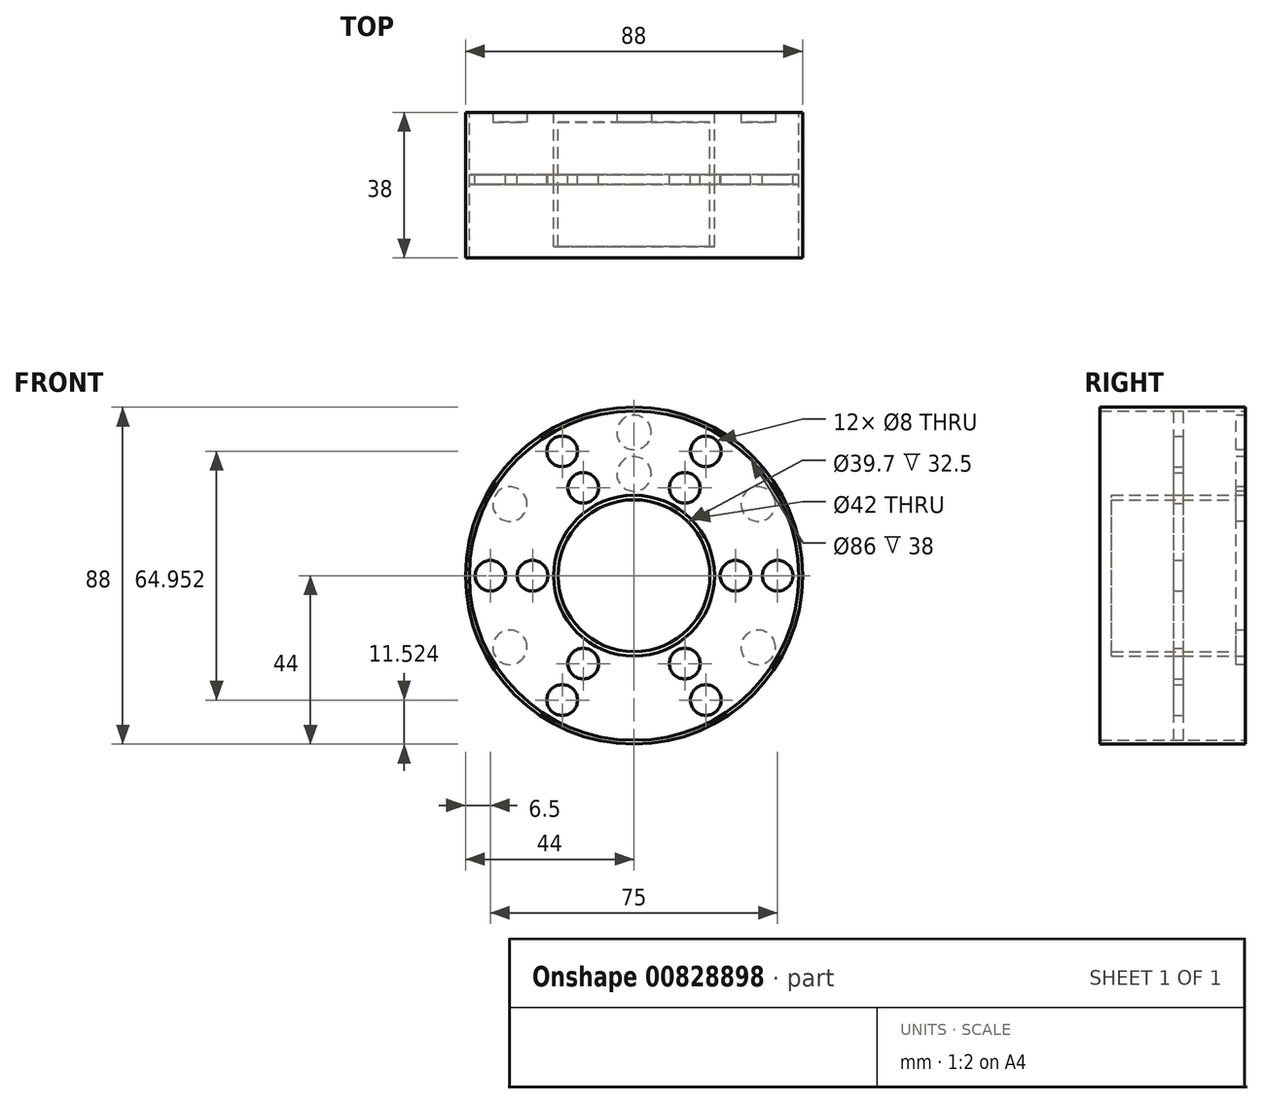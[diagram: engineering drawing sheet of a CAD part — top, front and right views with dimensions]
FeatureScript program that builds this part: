
annotation { "Feature Type Name" : "Feature", "Feature Type Description" : "" }
export const myFeature = defineFeature(function(context is Context, id is Id, definition is map)
    precondition{}
    {
        {
            var Q0;
            Q0=qCreatedBy(makeId("Front.planeOp"),FACE);
            var sketch = newSketch(context, id + "F0", { "sketchPlane" : qUnion([Q0])});
            skCircle(sketch, "E0", {"center": v(0, 0) * mm, "radius": 44 * mm});
            skCircle(sketch, "E1", {"center": v(0, 0) * mm, "radius": 19.85 * mm});
            skCircle(sketch, "E2", {"center": v(0, 0) * mm, "radius": 21 * mm});
            skCircle(sketch, "E3", {"center": v(0, 0) * mm, "radius": 43 * mm});
            skSolve(sketch);
        }
        {
            var Q0;
            Q0=makeQuery(id+"F0.imprint","IMPRINT",FACE,{"disambiguationData":[TD([[makeQuery(id+"F0.imprint","IMPRINT",EDGE,{"derivedFrom":sQuery(id+"F0.wireOp",EDGE,"E0")}),1.0]])]});
            extrude(context, id + "F1", {"entities" : qUnion([Q0]), "depth" : 38 * mm, "offsetDistance" : 25.4 * mm});
        }
        {
            var Q0;
            Q0=makeQuery(id+"F0.imprint","IMPRINT",FACE,{"disambiguationData":[TD([[makeQuery(id+"F0.imprint","IMPRINT",EDGE,{"derivedFrom":sQuery(id+"F0.wireOp",EDGE,"E2")}),-1.0]])]});
            extrude(context, id + "F2", {"entities" : qUnion([Q0]), "operationType" : NewBodyOperationType.ADD, "depth" : 2.5 * mm, "offsetDistance" : 25.4 * mm});
        }
        {
            var Q0;
            Q0=makeQuery(id+"F0.imprint","IMPRINT",FACE,{"disambiguationData":[TD([[makeQuery(id+"F0.imprint","IMPRINT",EDGE,{"derivedFrom":sQuery(id+"F0.wireOp",EDGE,"E1")}),-1.0]])]});
            extrude(context, id + "F3", {"entities" : qUnion([Q0]), "operationType" : NewBodyOperationType.ADD, "depth" : 35 * mm, "offsetDistance" : 25.4 * mm});
        }
        {
            var Q0;
            Q0=makeQuery(id+"F0.imprint","IMPRINT",FACE,{"disambiguationData":[TD([[makeQuery(id+"F0.imprint","IMPRINT",EDGE,{"derivedFrom":sQuery(id+"F0.wireOp",EDGE,"E1")}),1.0]])]});
            extrude(context, id + "F4", {"entities" : qUnion([Q0]), "operationType" : NewBodyOperationType.ADD, "depth" : 2.5 * mm, "offsetDistance" : 25.4 * mm});
        }
        {
            var Q0;
            Q0=makeQuery(id+"F2.opExtrude","CAP_FACE",FACE,{"disambiguationData":[OSD([sQuery(id+"F0.wireOp",EDGE,"E2"),sQuery(id+"F0.wireOp",EDGE,"E3")])],"isStart":false});
            var sketch = newSketch(context, id + "F5", { "sketchPlane" : qUnion([Q0])});
            skLineSegment(sketch, "E4", {"start": v(0, 0) * mm, "end": v(0, 43) * mm});
            skLineSegment(sketch, "E5", {"start": v(0, 0) * mm, "end": v(43, 0) * mm});
            skLineSegment(sketch, "E6", {"start": v(0, 0) * mm, "end": v(0, -43) * mm});
            skLineSegment(sketch, "E7", {"start": v(0, 0) * mm, "end": v(-43, 0) * mm});
            skPoint(sketch, "E8", {"position": v(0, 21) * mm});
            skLineSegment(sketch, "E9", {"start": v(0, 43) * mm, "end": v(0, 21) * mm});
            skPoint(sketch, "E10", {"position": v(0, 32) * mm});
            skPoint(sketch, "E11", {"position": v(0, 26.58) * mm});
            skCircle(sketch, "E12", {"center": v(0, 26.58) * mm, "radius": 4.5 * mm});
            skCircle(sketch, "E13.MirrorC", {"center": v(0, 37.42) * mm, "radius": 4.5 * mm});
            skPoint(sketch, "E14", {"position": v(21, 0) * mm});
            skLineSegment(sketch, "E15", {"start": v(43, 0) * mm, "end": v(21, 0) * mm});
            skCircle(sketch, "E16.1.0", {"center": v(32.41, 18.71) * mm, "radius": 4.5 * mm});
            skCircle(sketch, "E16.1.1", {"center": v(23.02, 13.29) * mm, "radius": 4.5 * mm});
            skCircle(sketch, "E16.2.0", {"center": v(32.41, -18.71) * mm, "radius": 4.5 * mm});
            skCircle(sketch, "E16.2.1", {"center": v(23.02, -13.29) * mm, "radius": 4.5 * mm});
            skCircle(sketch, "E16.3.0", {"center": v(0, -37.42) * mm, "radius": 4.5 * mm});
            skCircle(sketch, "E16.3.1", {"center": v(0, -26.58) * mm, "radius": 4.5 * mm});
            skCircle(sketch, "E16.4.0", {"center": v(-32.41, -18.71) * mm, "radius": 4.5 * mm});
            skCircle(sketch, "E16.4.1", {"center": v(-23.02, -13.29) * mm, "radius": 4.5 * mm});
            skCircle(sketch, "E16.5.0", {"center": v(-32.41, 18.71) * mm, "radius": 4.5 * mm});
            skCircle(sketch, "E16.5.1", {"center": v(-23.02, 13.29) * mm, "radius": 4.5 * mm});
            skPoint(sketch, "E16.center", {"position": v(0, 0) * mm});
            skLineSegment(sketch, "E16.anchor1", {"start": v(0, 0) * mm, "end": v(0, 37.42) * mm, "construction": true});
            skLineSegment(sketch, "E16.anchor2", {"start": v(0, 0) * mm, "end": v(-32.41, 18.71) * mm, "construction": true});
            skSolve(sketch);
        }
        {
            var Q0;
            Q0=makeQuery(id+"F5.imprint","IMPRINT",FACE,{"disambiguationData":[TD([[makeQuery(id+"F5.imprint","IMPRINT",EDGE,{"derivedFrom":sQuery(id+"F5.wireOp",EDGE,"E16.1.0")}),-1.0]])]});
            var Q1;
            Q1=makeQuery(id+"F5.imprint","IMPRINT",FACE,{"disambiguationData":[TD([[makeQuery(id+"F5.imprint","IMPRINT",EDGE,{"derivedFrom":sQuery(id+"F5.wireOp",EDGE,"E16.1.1")}),1.0]])]});
            var Q2;
            Q2=makeQuery(id+"F5.imprint","IMPRINT",FACE,{"disambiguationData":[TD([[makeQuery(id+"F5.imprint","IMPRINT",EDGE,{"derivedFrom":sQuery(id+"F5.wireOp",EDGE,"E16.2.1")}),1.0]])]});
            var Q3;
            Q3=makeQuery(id+"F5.imprint","IMPRINT",FACE,{"disambiguationData":[TD([[makeQuery(id+"F5.imprint","IMPRINT",EDGE,{"derivedFrom":sQuery(id+"F5.wireOp",EDGE,"E16.2.0")}),-1.0]])]});
            var Q4;
            {var subQ0=sQuery(id+"F5.wireOp",EDGE,"E16.3.0");var subQ1=sQuery(id+"F5.wireOp",EDGE,"E6");var subQ2=makeQuery(id+"F5.imprint","INTERSECT",VERTEX,{"disambiguationData":[OD(0.0)],"derivedFrom":[subQ1,subQ0]});Q4=makeQuery(id+"F5.imprint","IMPRINT",FACE,{"disambiguationData":[TD([[makeQuery(id+"F5.imprint","IMPRINT",EDGE,{"disambiguationData":[TD([[subQ2,-1.0]])],"derivedFrom":subQ1}),1.0]])]});}
            var Q5;
            {var subQ0=sQuery(id+"F5.wireOp",EDGE,"E16.3.0");var subQ1=sQuery(id+"F5.wireOp",EDGE,"E6");var subQ2=makeQuery(id+"F5.imprint","INTERSECT",VERTEX,{"disambiguationData":[OD(0.0)],"derivedFrom":[subQ1,subQ0]});Q5=makeQuery(id+"F5.imprint","IMPRINT",FACE,{"disambiguationData":[TD([[makeQuery(id+"F5.imprint","IMPRINT",EDGE,{"disambiguationData":[TD([[subQ2,-1.0]])],"derivedFrom":subQ1}),-1.0]])]});}
            var Q6;
            {var subQ0=sQuery(id+"F5.wireOp",EDGE,"E16.3.1");var subQ1=sQuery(id+"F5.wireOp",EDGE,"E6");var subQ2=makeQuery(id+"F5.imprint","INTERSECT",VERTEX,{"disambiguationData":[OD(0.0)],"derivedFrom":[subQ1,subQ0]});Q6=makeQuery(id+"F5.imprint","IMPRINT",FACE,{"disambiguationData":[TD([[makeQuery(id+"F5.imprint","IMPRINT",EDGE,{"disambiguationData":[TD([[subQ2,-1.0]])],"derivedFrom":subQ1}),-1.0]])]});}
            var Q7;
            {var subQ0=sQuery(id+"F5.wireOp",EDGE,"E16.3.1");var subQ1=sQuery(id+"F5.wireOp",EDGE,"E6");var subQ2=makeQuery(id+"F5.imprint","INTERSECT",VERTEX,{"disambiguationData":[OD(0.0)],"derivedFrom":[subQ1,subQ0]});Q7=makeQuery(id+"F5.imprint","IMPRINT",FACE,{"disambiguationData":[TD([[makeQuery(id+"F5.imprint","IMPRINT",EDGE,{"disambiguationData":[TD([[subQ2,-1.0]])],"derivedFrom":subQ1}),1.0]])]});}
            var Q8;
            Q8=makeQuery(id+"F5.imprint","IMPRINT",FACE,{"disambiguationData":[TD([[makeQuery(id+"F5.imprint","IMPRINT",EDGE,{"derivedFrom":sQuery(id+"F5.wireOp",EDGE,"E16.4.1")}),1.0]])]});
            var Q9;
            Q9=makeQuery(id+"F5.imprint","IMPRINT",FACE,{"disambiguationData":[TD([[makeQuery(id+"F5.imprint","IMPRINT",EDGE,{"derivedFrom":sQuery(id+"F5.wireOp",EDGE,"E16.4.0")}),-1.0]])]});
            var Q10;
            Q10=makeQuery(id+"F5.imprint","IMPRINT",FACE,{"disambiguationData":[TD([[makeQuery(id+"F5.imprint","IMPRINT",EDGE,{"derivedFrom":sQuery(id+"F5.wireOp",EDGE,"E16.5.0")}),-1.0]])]});
            var Q11;
            Q11=makeQuery(id+"F5.imprint","IMPRINT",FACE,{"disambiguationData":[TD([[makeQuery(id+"F5.imprint","IMPRINT",EDGE,{"derivedFrom":sQuery(id+"F5.wireOp",EDGE,"E16.5.1")}),1.0]])]});
            var Q12;
            {var subQ0=sQuery(id+"F5.wireOp",EDGE,"E12");var subQ1=sQuery(id+"F5.wireOp",EDGE,"E9");var subQ2=makeQuery(id+"F5.imprint","INTERSECT",VERTEX,{"disambiguationData":[OD(0.0)],"derivedFrom":[subQ1,subQ0]});Q12=makeQuery(id+"F5.imprint","IMPRINT",FACE,{"disambiguationData":[TD([[makeQuery(id+"F5.imprint","IMPRINT",EDGE,{"disambiguationData":[TD([[subQ2,-1.0]])],"derivedFrom":subQ1}),-1.0]])]});}
            var Q13;
            {var subQ0=sQuery(id+"F5.wireOp",EDGE,"E12");var subQ1=sQuery(id+"F5.wireOp",EDGE,"E9");var subQ2=makeQuery(id+"F5.imprint","INTERSECT",VERTEX,{"disambiguationData":[OD(0.0)],"derivedFrom":[subQ1,subQ0]});Q13=makeQuery(id+"F5.imprint","IMPRINT",FACE,{"disambiguationData":[TD([[makeQuery(id+"F5.imprint","IMPRINT",EDGE,{"disambiguationData":[TD([[subQ2,-1.0]])],"derivedFrom":subQ1}),1.0]])]});}
            var Q14;
            {var subQ0=sQuery(id+"F5.wireOp",EDGE,"E13.MirrorC");var subQ1=sQuery(id+"F5.wireOp",EDGE,"E9");var subQ2=makeQuery(id+"F5.imprint","INTERSECT",VERTEX,{"disambiguationData":[OD(0.0)],"derivedFrom":[subQ1,subQ0]});Q14=makeQuery(id+"F5.imprint","IMPRINT",FACE,{"disambiguationData":[TD([[makeQuery(id+"F5.imprint","IMPRINT",EDGE,{"disambiguationData":[TD([[subQ2,-1.0]])],"derivedFrom":subQ1}),1.0]])]});}
            var Q15;
            {var subQ0=sQuery(id+"F5.wireOp",EDGE,"E13.MirrorC");var subQ1=sQuery(id+"F5.wireOp",EDGE,"E9");var subQ2=makeQuery(id+"F5.imprint","INTERSECT",VERTEX,{"disambiguationData":[OD(0.0)],"derivedFrom":[subQ1,subQ0]});Q15=makeQuery(id+"F5.imprint","IMPRINT",FACE,{"disambiguationData":[TD([[makeQuery(id+"F5.imprint","IMPRINT",EDGE,{"disambiguationData":[TD([[subQ2,-1.0]])],"derivedFrom":subQ1}),-1.0]])]});}
            extrude(context, id + "F6", {"entities" : qUnion([Q0, Q1, Q2, Q3, Q4, Q5, Q6, Q7, Q8, Q9, Q10, Q11, Q12, Q13, Q14, Q15]), "operationType" : NewBodyOperationType.REMOVE, "oppositeDirection" : true, "depth" : 12.7 * mm, "offsetDistance" : 25.4 * mm});
        }
        {
            var Q0;
            Q0=qCreatedBy(makeId("Front.planeOp"),FACE);
            var sketch = newSketch(context, id + "F7", { "sketchPlane" : qUnion([Q0])});
            skCircle(sketch, "E17", {"center": v(0, 0) * mm, "radius": 21 * mm});
            skCircle(sketch, "E18", {"center": v(0, 0) * mm, "radius": 43 * mm});
            skLineSegment(sketch, "E19", {"start": v(-21, 0) * mm, "end": v(-43, 0) * mm});
            skPoint(sketch, "E20", {"position": v(-32, 0) * mm});
            skLineSegment(sketch, "E21", {"start": v(-32, 0) * mm, "end": v(-21, 0) * mm});
            skPoint(sketch, "E22", {"position": v(-26.5, 0) * mm});
            skCircle(sketch, "E23", {"center": v(-26.5, 0) * mm, "radius": 4 * mm});
            skCircle(sketch, "E24.MirrorC", {"center": v(-37.5, 0) * mm, "radius": 4 * mm});
            skCircle(sketch, "E25.1.0", {"center": v(-18.75, 32.48) * mm, "radius": 4 * mm});
            skCircle(sketch, "E25.1.1", {"center": v(-13.25, 22.95) * mm, "radius": 4 * mm});
            skCircle(sketch, "E25.2.0", {"center": v(18.75, 32.48) * mm, "radius": 4 * mm});
            skCircle(sketch, "E25.2.1", {"center": v(13.25, 22.95) * mm, "radius": 4 * mm});
            skCircle(sketch, "E25.3.0", {"center": v(37.5, 0) * mm, "radius": 4 * mm});
            skCircle(sketch, "E25.3.1", {"center": v(26.5, 0) * mm, "radius": 4 * mm});
            skCircle(sketch, "E25.4.0", {"center": v(18.75, -32.48) * mm, "radius": 4 * mm});
            skCircle(sketch, "E25.4.1", {"center": v(13.25, -22.95) * mm, "radius": 4 * mm});
            skCircle(sketch, "E25.5.0", {"center": v(-18.75, -32.48) * mm, "radius": 4 * mm});
            skCircle(sketch, "E25.5.1", {"center": v(-13.25, -22.95) * mm, "radius": 4 * mm});
            skLineSegment(sketch, "E25.anchor1", {"start": v(0, 0) * mm, "end": v(-37.5, 0) * mm, "construction": true});
            skLineSegment(sketch, "E25.anchor2", {"start": v(0, 0) * mm, "end": v(-18.75, -32.48) * mm, "construction": true});
            skSolve(sketch);
        }
        {
            var Q0;
            Q0=makeQuery(id+"F7.imprint","IMPRINT",FACE,{"disambiguationData":[TD([[makeQuery(id+"F7.imprint","IMPRINT",EDGE,{"derivedFrom":sQuery(id+"F7.wireOp",EDGE,"E17")}),-1.0]])]});
            extrude(context, id + "F8", {"entities" : qUnion([Q0]), "depth" : 2.5 * mm, "offsetDistance" : 25.4 * mm});
        }
        {
            var Q0;
            Q0=makeQuery(id+"F8.opExtrude","SWEPT_BODY",BODY,{"disambiguationData":[OSD([sQuery(id+"F7.wireOp",EDGE,"E17"),sQuery(id+"F7.wireOp",EDGE,"E18"),sQuery(id+"F7.wireOp",EDGE,"E23"),sQuery(id+"F7.wireOp",EDGE,"E24.MirrorC"),sQuery(id+"F7.wireOp",EDGE,"E25.1.0"),sQuery(id+"F7.wireOp",EDGE,"E25.1.1"),sQuery(id+"F7.wireOp",EDGE,"E25.2.0"),sQuery(id+"F7.wireOp",EDGE,"E25.2.1"),sQuery(id+"F7.wireOp",EDGE,"E25.3.0"),sQuery(id+"F7.wireOp",EDGE,"E25.3.1"),sQuery(id+"F7.wireOp",EDGE,"E25.4.0"),sQuery(id+"F7.wireOp",EDGE,"E25.4.1"),sQuery(id+"F7.wireOp",EDGE,"E25.5.0"),sQuery(id+"F7.wireOp",EDGE,"E25.5.1")])]});
            transform(context, id + "F9", {"entities" : qUnion([Q0]), "transformType" : TransformType.TRANSLATION_3D, "dx" : 0 * mm, "dy" : -16.26 * mm, "dz" : 0 * mm, "makeCopy" : false});
        }
    });
